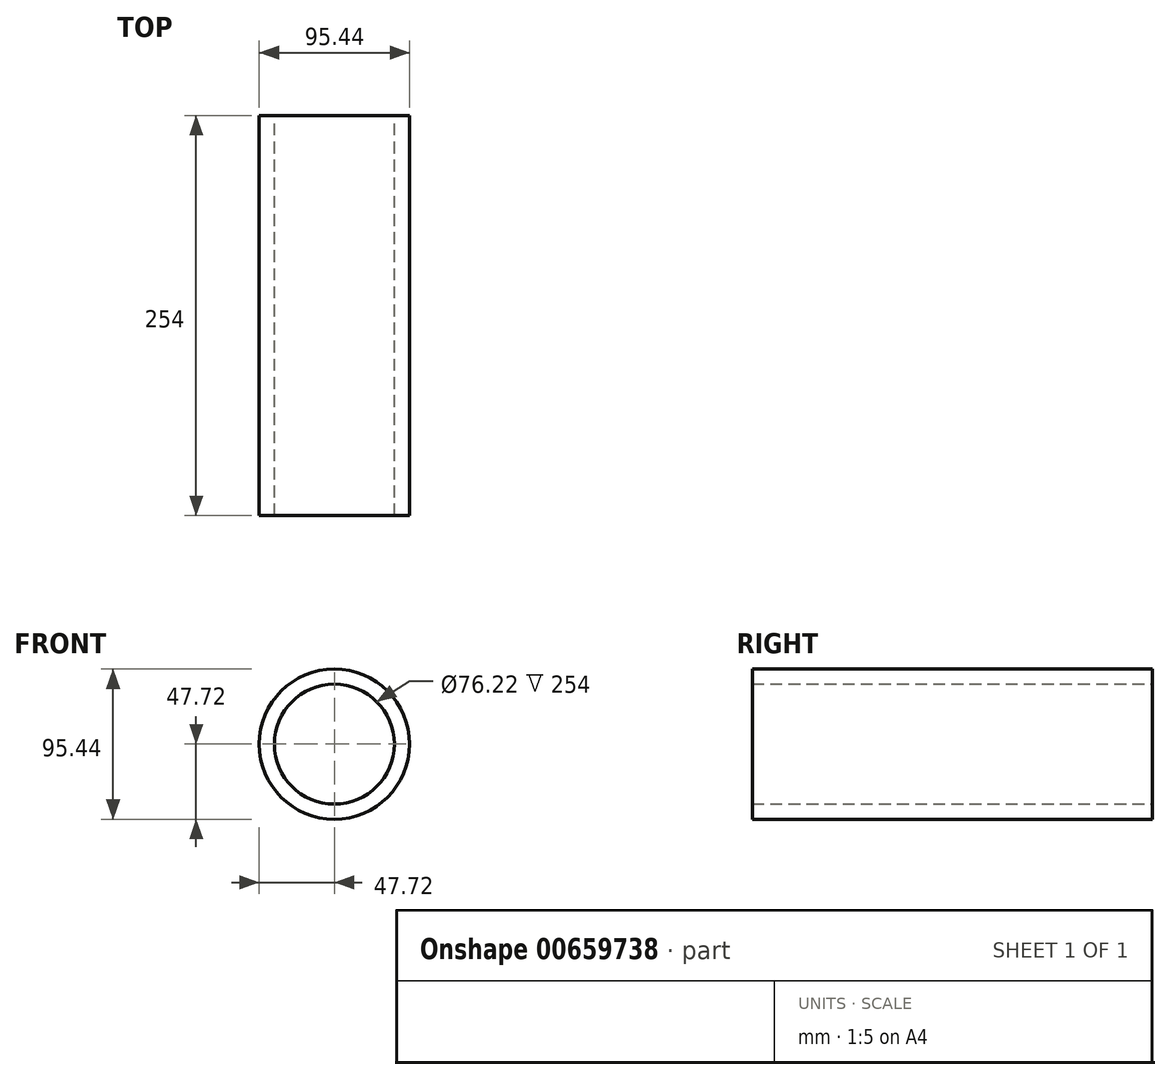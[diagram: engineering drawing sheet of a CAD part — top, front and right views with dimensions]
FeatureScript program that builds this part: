
annotation { "Feature Type Name" : "Feature", "Feature Type Description" : "" }
export const myFeature = defineFeature(function(context is Context, id is Id, definition is map)
    precondition{}
    {
        {
            var Q0;
            Q0=qCreatedBy(makeId("Front.planeOp"),FACE);
            var sketch = newSketch(context, id + "F0", { "sketchPlane" : qUnion([Q0])});
            skCircle(sketch, "E0", {"center": v(0, 0) * mm, "radius": 47.72 * mm});
            skCircle(sketch, "E1", {"center": v(0, 0) * mm, "radius": 38.11 * mm});
            skSolve(sketch);
        }
        {
            var Q0;
            Q0=makeQuery(id+"F0.imprint","IMPRINT",FACE,{"disambiguationData":[TD([[makeQuery(id+"F0.imprint","IMPRINT",EDGE,{"derivedFrom":sQuery(id+"F0.wireOp",EDGE,"E0")}),1.0]])]});
            extrude(context, id + "F1", {"entities" : qUnion([Q0]), "depth" : 254 * mm, "offsetDistance" : 25.4 * mm});
        }
    });
